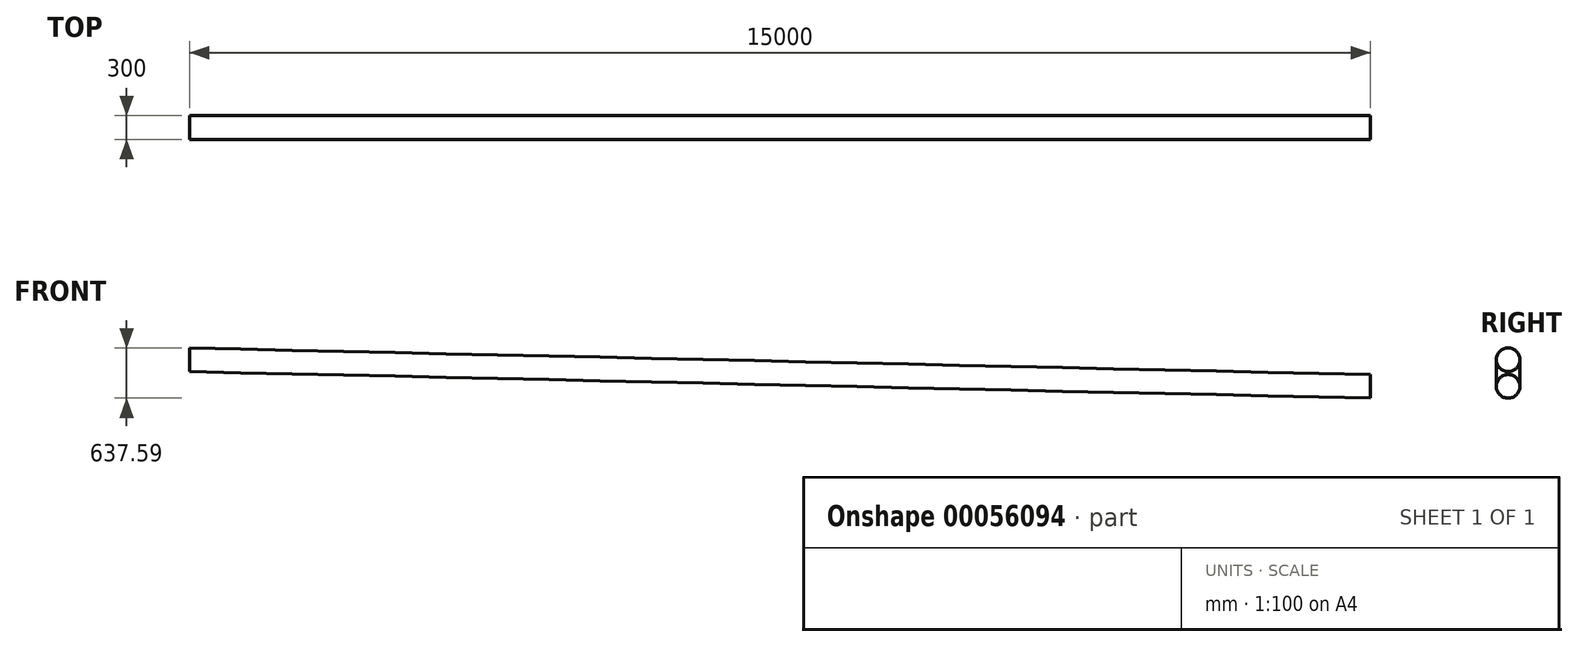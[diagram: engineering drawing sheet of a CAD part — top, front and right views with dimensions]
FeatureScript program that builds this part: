
annotation { "Feature Type Name" : "Feature", "Feature Type Description" : "" }
export const myFeature = defineFeature(function(context is Context, id is Id, definition is map)
    precondition{}
    {
        {
            var Q0;
            Q0=qCreatedBy(makeId("Right.planeOp"),FACE);
            var sketch = newSketch(context, id + "F0", { "sketchPlane" : qUnion([Q0])});
            skCircle(sketch, "E0", {"center": v(0, 0) * mm, "radius": 150 * mm});
            skSolve(sketch);
        }
        {
            var Q0;
            Q0=qCreatedBy(makeId("Front.planeOp"),FACE);
            var sketch = newSketch(context, id + "F1", { "sketchPlane" : qUnion([Q0])});
            skLineSegment(sketch, "E1", {"start": v(0, 0) * mm, "end": v(15000, -337.59) * mm});
            skSolve(sketch);
        }
        {
            var Q0;
            Q0=makeQuery(id+"F0.imprint","IMPRINT",FACE,{"disambiguationData":[TD([[makeQuery(id+"F0.imprint","IMPRINT",EDGE,{"derivedFrom":sQuery(id+"F0.wireOp",EDGE,"E0")}),1.0]])]});
            var Q1;
            Q1=sQuery(id+"F1.wireOp",EDGE,"E1");
            sweep(context, id + "F2", {"profiles" : qUnion([Q0]), "path" : qUnion([Q1])});
        }
    });
